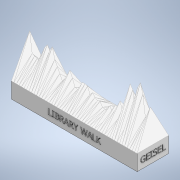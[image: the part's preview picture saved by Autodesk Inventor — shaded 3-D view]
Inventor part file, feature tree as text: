
AUTODESK INVENTOR PART (.ipt)
format: ipt  version: 2020.1 (Build 241239000, 239)  size: 1,961,984 bytes
history: native  units: in
note: dims shown in document units (in); Inventor stores cm internally (conversion verified against a paired STEP export)
features: extrude x5, sketch x5, projected_geometry x3, other x2
ambient origin geometry x8: Origin, YZ Plane, XZ Plane, XY Plane, X Axis, Y Axis, Z Axis, Center Point
bodies: Solid1 (feature_tree)
feature tree (15):
  other  "test"
  extrude  "Extrusion1"  Depth=8.0in
  extrude  "Extrusion2"  Depth=4.0in
  extrude  "Extrusion3"  Depth=0.34in
  extrude  "Extrusion4"  Depth=0.2in TaperAngle=0.0deg
  extrude  "Extrusion5"  Depth=1.0in
  sketch  "Sketch1"  dims[d0=1.0in d1=0.0in d2=8.0in]
  sketch  "Sketch2"  dims[d3=1.0in d4=4.0in]
  projected_geometry  "Projected Loop1"
  sketch  "Sketch3"  dims[d5=0.32in d6=0.34in]
  projected_geometry  "Projected Loop2"
  sketch  "Sketch4"  dims[d7=2.0in d8=0.2in d9=0.0in]
  projected_geometry  "Projected Loop3"
  sketch  "Sketch5"  dims[d10=2.0in d11=1.0in d12=1.5in d13=0.6in d14=0.25in d15=0.2in d16=0.2in d17=0.0in d18=8.0in d19=0.4in d20=0.0in d21=1.0in d22=0.3in d23=0.2in d24=0.0in d25=8.0in d26=2.0in d27=1.8in d28=0.1in d29=0.3333in d30=4.0in d31=3.0in d32=0.5in d33=1.0in d34=0.3333in d35=0.2in d36=0.0in]
  other  "MeshFeature1"
